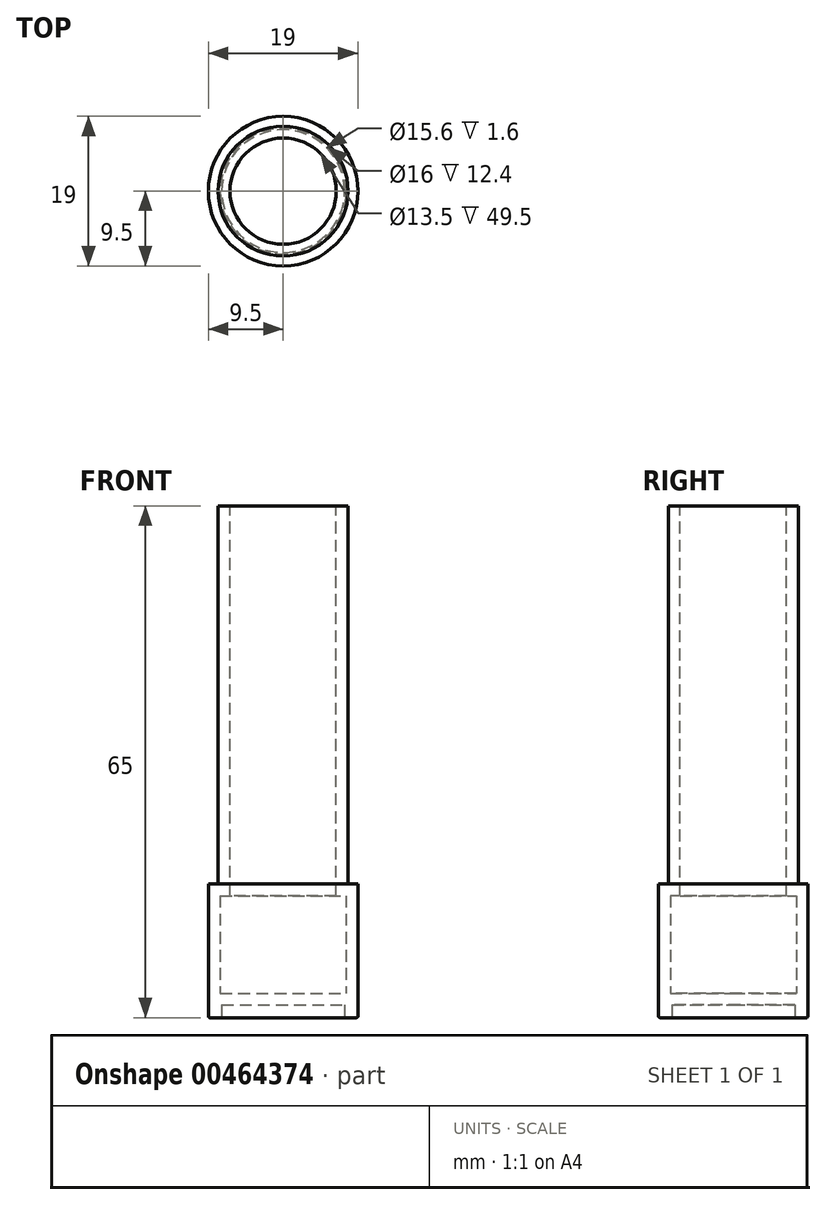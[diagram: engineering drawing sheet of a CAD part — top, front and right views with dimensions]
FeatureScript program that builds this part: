
annotation { "Feature Type Name" : "Feature", "Feature Type Description" : "" }
export const myFeature = defineFeature(function(context is Context, id is Id, definition is map)
    precondition{}
    {
        {
            var Q0;
            Q0=qCreatedBy(makeId("Top.planeOp"),FACE);
            var sketch = newSketch(context, id + "F0", { "sketchPlane" : qUnion([Q0])});
            skCircle(sketch, "E0", {"center": v(0, 0) * mm, "radius": 9.5 * mm});
            skSolve(sketch);
        }
        {
            var Q0;
            Q0 = qSketchRegion(id + "F0", true);
            extrude(context, id + "F1", {"entities" : qUnion([Q0]), "depth" : 65 * mm});
        }
        {
            var Q0;
            Q0=makeQuery(id+"F1.opExtrude","CAP_EDGE",EDGE,{"disambiguationData":[OSD([sQuery(id+"F0.wireOp",EDGE,"E0")])],"isStart":true});
            fillet(context, id + "F2", {"entities" : qUnion([Q0]), "radius" : 0.2 * mm, "tangentPropagation" : true, "allowEdgeOverflow" : false});
        }
        {
            var Q0;
            Q0=makeQuery(id+"F1.opExtrude","CAP_FACE",FACE,{"disambiguationData":[OSD([sQuery(id+"F0.wireOp",EDGE,"E0")])],"isStart":false});
            var sketch = newSketch(context, id + "F3", { "sketchPlane" : qUnion([Q0])});
            skCircle(sketch, "E1", {"center": v(0, 0) * mm, "radius": 8.25 * mm});
            skSolve(sketch);
        }
        {
            var Q0;
            Q0=makeQuery(id+"F3.imprint","IMPRINT",FACE,{"disambiguationData":[TD([[makeQuery(id+"F3.imprint","IMPRINT",EDGE,{"derivedFrom":sQuery(id+"F3.wireOp",EDGE,"E1")}),-1.0]])]});
            extrude(context, id + "F4", {"entities" : qUnion([Q0]), "operationType" : NewBodyOperationType.REMOVE, "oppositeDirection" : true, "depth" : 48 * mm});
        }
        {
            var Q0;
            Q0=makeQuery(id+"F1.opExtrude","CAP_FACE",FACE,{"disambiguationData":[OSD([sQuery(id+"F0.wireOp",EDGE,"E0")])],"isStart":true});
            var sketch = newSketch(context, id + "F5", { "sketchPlane" : qUnion([Q0])});
            skCircle(sketch, "E2", {"center": v(0, 0) * mm, "radius": 7.8 * mm});
            skSolve(sketch);
        }
        {
            var Q0;
            Q0 = qSketchRegion(id + "F5", true);
            extrude(context, id + "F6", {"entities" : qUnion([Q0]), "operationType" : NewBodyOperationType.REMOVE, "oppositeDirection" : true, "depth" : 1.6 * mm});
        }
        {
            var Q0;
            Q0=makeQuery(id+"F1.opExtrude","CAP_FACE",FACE,{"disambiguationData":[OSD([sQuery(id+"F0.wireOp",EDGE,"E0")])],"isStart":false});
            shell(context, id + "F7", {"entities" : qUnion([Q0]), "thickness" : 1.5 * mm});
        }
    });
